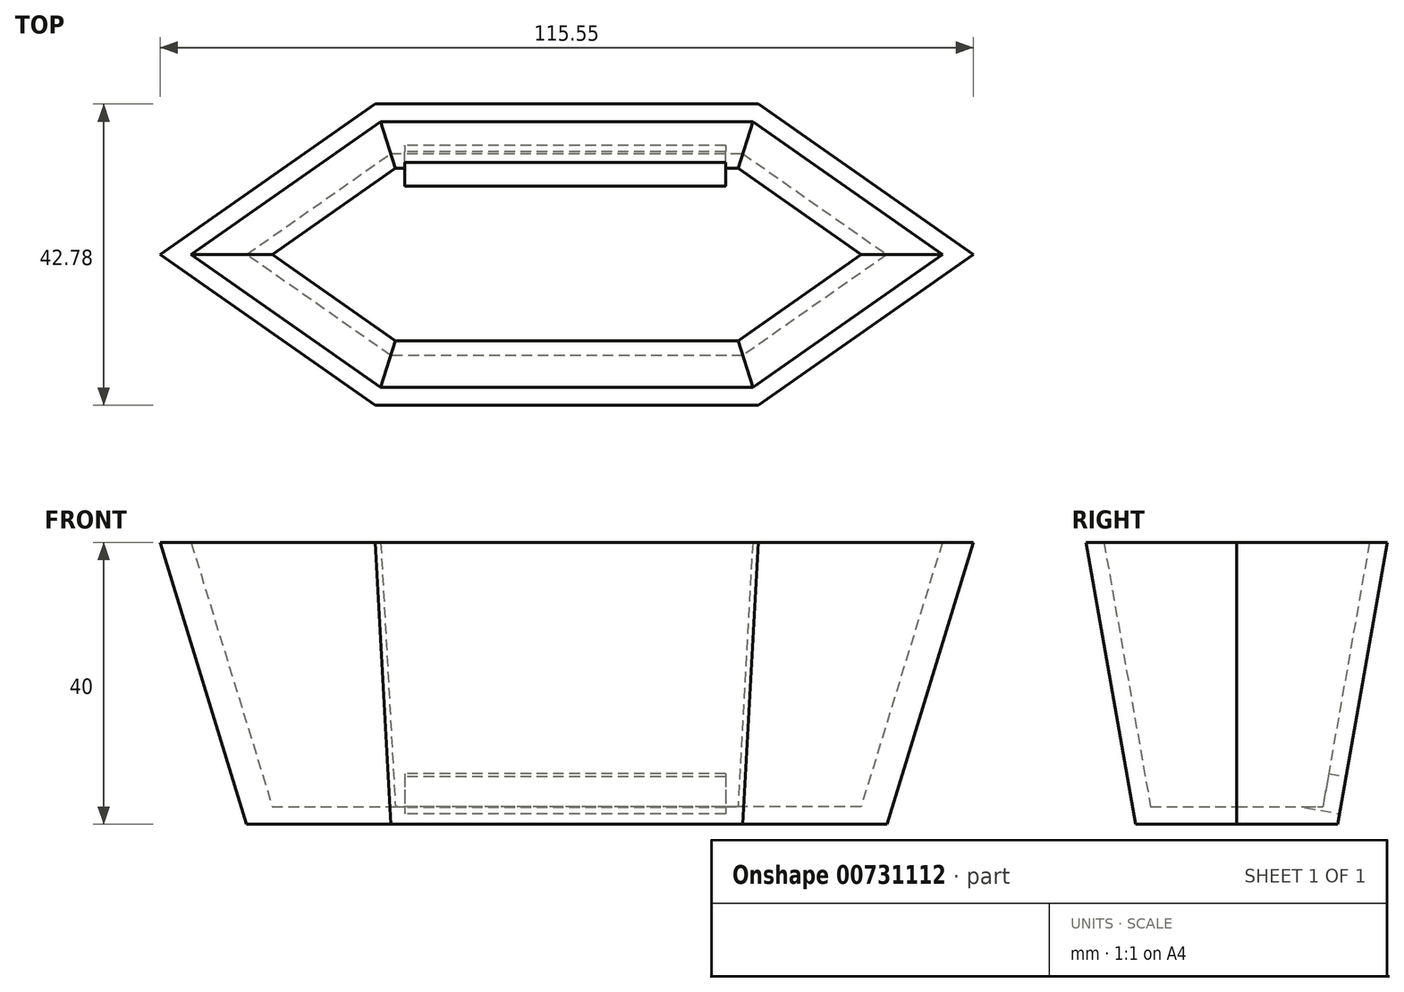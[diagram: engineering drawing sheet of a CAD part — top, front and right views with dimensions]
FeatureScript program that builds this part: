
annotation { "Feature Type Name" : "Feature", "Feature Type Description" : "" }
export const myFeature = defineFeature(function(context is Context, id is Id, definition is map)
    precondition{}
    {
        {
            var Q0;
            Q0=qCreatedBy(makeId("Top.planeOp"),FACE);
            var sketch = newSketch(context, id + "F0", { "sketchPlane" : qUnion([Q0])});
            skLineSegment(sketch, "E0", {"start": v(0, 0) * mm, "end": v(24.82, 0) * mm});
            skLineSegment(sketch, "E1", {"start": v(0, 0) * mm, "end": v(-25.18, 0) * mm});
            skLineSegment(sketch, "E2", {"start": v(24.82, 0) * mm, "end": v(45.3, -14.34) * mm});
            skLineSegment(sketch, "E3", {"start": v(45.3, -14.34) * mm, "end": v(24.82, -28.68) * mm});
            skLineSegment(sketch, "E4", {"start": v(24.82, -28.68) * mm, "end": v(-25.18, -28.68) * mm});
            skLineSegment(sketch, "E5", {"start": v(-25.18, -28.68) * mm, "end": v(-45.66, -14.34) * mm});
            skLineSegment(sketch, "E6", {"start": v(-45.66, -14.34) * mm, "end": v(-25.18, 0) * mm});
            skSolve(sketch);
        }
        {
            var Q0;
            Q0=makeQuery(id+"F0.imprint","IMPRINT",FACE,{"disambiguationData":[TD([[makeQuery(id+"F0.imprint","IMPRINT",EDGE,{"derivedFrom":sQuery(id+"F0.wireOp",EDGE,"E0")}),-1.0]])]});
            extrude(context, id + "F1", {"entities" : qUnion([Q0]), "depth" : 40 * mm, "offsetDistance" : 25 * mm, "hasDraft" : true, "draftAngle" : 10 * degree});
        }
        {
            var Q0;
            Q0=makeQuery(id+"F1.opExtrude","CAP_FACE",FACE,{"disambiguationData":[OSD([sQuery(id+"F0.wireOp",EDGE,"E0"),sQuery(id+"F0.wireOp",EDGE,"E1"),sQuery(id+"F0.wireOp",EDGE,"E2"),sQuery(id+"F0.wireOp",EDGE,"E3"),sQuery(id+"F0.wireOp",EDGE,"E4"),sQuery(id+"F0.wireOp",EDGE,"E5"),sQuery(id+"F0.wireOp",EDGE,"E6")])],"isStart":false});
            shell(context, id + "F2", {"entities" : qUnion([Q0]), "thickness" : 2.5 * mm});
        }
        {
            var Q0;
            Q0=makeQuery(id+"F1.opExtrude","SWEPT_FACE",FACE,{"disambiguationData":[OSD([sQuery(id+"F0.wireOp",EDGE,"E0"),sQuery(id+"F0.wireOp",EDGE,"E1")])]});
            var sketch = newSketch(context, id + "F3", { "sketchPlane" : qUnion([Q0])});
            skLineSegment(sketch, "E7.bottom", {"start": v(-22.37, 6.84) * mm, "end": v(23.21, 6.84) * mm});
            skLineSegment(sketch, "E7.top", {"start": v(-22.37, 1.49) * mm, "end": v(23.21, 1.49) * mm});
            skLineSegment(sketch, "E7.left", {"start": v(-22.37, 6.84) * mm, "end": v(-22.37, 1.49) * mm});
            skLineSegment(sketch, "E7.right", {"start": v(23.21, 6.84) * mm, "end": v(23.21, 1.49) * mm});
            skSolve(sketch);
        }
        {
            var Q0;
            Q0=makeQuery(id+"F3.imprint","IMPRINT",FACE,{"disambiguationData":[TD([[makeQuery(id+"F3.imprint","IMPRINT",EDGE,{"derivedFrom":sQuery(id+"F3.wireOp",EDGE,"E7.bottom")}),-1.0]])]});
            extrude(context, id + "F4", {"entities" : qUnion([Q0]), "operationType" : NewBodyOperationType.REMOVE, "oppositeDirection" : true, "depth" : 5 * mm, "offsetDistance" : 25 * mm});
        }
    });
